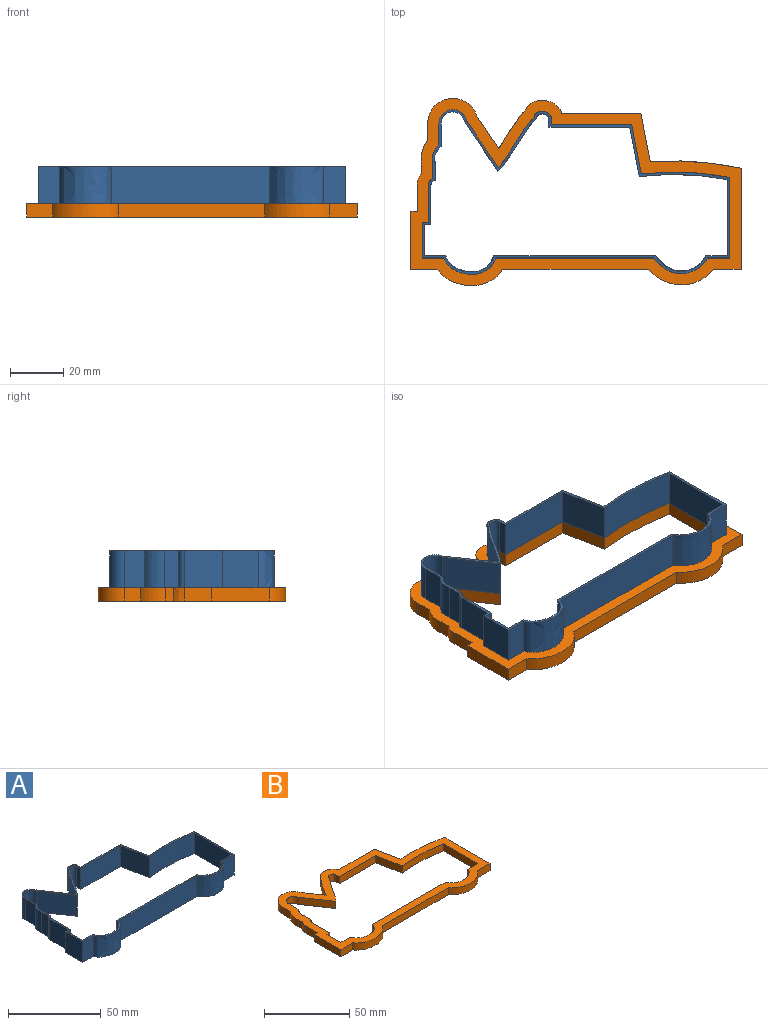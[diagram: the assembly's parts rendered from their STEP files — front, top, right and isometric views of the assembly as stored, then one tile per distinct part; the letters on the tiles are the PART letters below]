
ASSEMBLY  parts=2 mates=1
PART A: 44 faces, bbox 115.7x62.7x13.9 mm
  f0: extruded ~13.72x6.48mm, area 122.1mm2, adj f1,f20,f21,f22
  f1: extruded ~18.75x13.72mm, area 317mm2, adj f0,f2,f21,f22
  f2: plane 17.47x13.72mm, normal (0.83,0.56,0), area 289.6mm2, adj f1,f3,f21,f22
  f3: cylinder r=5.25mm len=13.72mm, axis (0,0,-1), area 215.1mm2, adj f2,f4,f21,f22
  f4: plane 13.72x7.81mm, normal (-1,0,0), area 107.1mm2, adj f3,f5,f21,f22
  f5: extruded ~13.72x7.16mm, area 108.1mm2, adj f4,f6,f21,f22
  f6: plane 13.72x5.4mm, normal (-1,0,0), area 74.1mm2, adj f5,f7,f21,f22
  f7: extruded ~13.72x2.32mm, area 40.1mm2, adj f6,f8,f21,f22
  f8: plane 14.17x13.72mm, normal (-1,0,0), area 194.4mm2, adj f7,f9,f21,f22
  f9: plane 13.72x2.46mm, normal (0,1,0), area 33.7mm2, adj f8,f10,f21,f22
  f10: plane 13.72x13.34mm, normal (-1,0,0), area 183mm2, adj f9,f11,f21,f22
  f11: plane 13.72x8.14mm, normal (0,-1,0), area 111.7mm2, adj f10,f12,f21,f22
  f12: extruded ~19.49x13.72mm, area 337.3mm2, adj f11,f13,f21,f22
  f13: plane 59.29x13.72mm, normal (0,-1,0), area 813.3mm2, adj f12,f14,f21,f22
  f14: extruded ~20.07x13.72mm, area 333.6mm2, adj f13,f15,f21,f22
  f15: plane 13.72x8.46mm, normal (0,-1,0), area 116.1mm2, adj f14,f16,f21,f22
  f16: plane 30.15x13.72mm, normal (1,0,0), area 413.6mm2, adj f15,f17,f21,f22
  f17: extruded ~33.27x13.72mm, area 458.6mm2, adj f16,f18,f21,f22
  f18: plane 18.41x13.72mm, normal (0.98,0.19,0), area 257.3mm2, adj f17,f19,f21,f22
  f19: plane 30.1x13.72mm, normal (0,1,0), area 412.8mm2, adj f18,f20,f21,f22
  f20: plane 13.72x2.38mm, normal (1,0,0), area 32.7mm2, adj f0,f19,f21,f22
  f21: plane 115.66x62.75mm, normal (0,0,1), area 320.1mm2, adj f0,f1,f2,f3,f4,f5,f6,f7
  f22: plane 115.66x62.75mm, normal (0,0,-1), area 320.1mm2, adj f0,f1,f2,f3,f4,f5,f6,f7
  f23: extruded ~13.72x4.72mm, area 89.5mm2, adj f21,f22,f24,f43
  f24: extruded ~19.72x14.45mm, area 336.3mm2, adj f21,f22,f23,f25
  f25: plane 18.5x13.72mm, normal (-0.83,-0.56,0), area 306.8mm2, adj f21,f22,f24,f26
  f26: cylinder r=4.36mm len=13.72mm, axis (0,0,-1), area 181.3mm2, adj f21,f22,f25,f27
  f27: plane 13.72x8.24mm, normal (1,0,0), area 113mm2, adj f21,f22,f26,f28
  f28: extruded ~13.72x6.65mm, area 101.9mm2, adj f21,f22,f27,f29
  f29: plane 13.72x6.21mm, normal (1,0,0), area 85.2mm2, adj f21,f22,f28,f30
  f30: extruded ~13.72x1.63mm, area 33.9mm2, adj f21,f22,f29,f31
  f31: plane 15.03x13.72mm, normal (1,0,0), area 206.1mm2, adj f21,f22,f30,f32
  f32: plane 13.72x2.46mm, normal (0,-1,0), area 33.7mm2, adj f21,f22,f31,f33
  f33: plane 13.72x11.56mm, normal (1,0,0), area 158.6mm2, adj f21,f22,f32,f34
  f34: plane 13.72x7.95mm, normal (0,1,0), area 109mm2, adj f21,f22,f33,f35
  f35: extruded ~18.14x13.72mm, area 324.1mm2, adj f21,f22,f34,f36
  f36: plane 60.41x13.72mm, normal (0,1,0), area 828.5mm2, adj f21,f22,f35,f37
  f37: extruded ~19.01x13.72mm, area 322mm2, adj f21,f22,f36,f38
  f38: plane 13.72x8.17mm, normal (0,1,0), area 112.1mm2, adj f21,f22,f37,f39
  f39: plane 28.53x13.72mm, normal (-1,0,0), area 391.3mm2, adj f21,f22,f38,f40
  f40: extruded ~33.1x13.72mm, area 456mm2, adj f21,f22,f39,f41
  f41: plane 18.5x13.72mm, normal (-0.98,-0.19,0), area 258.5mm2, adj f21,f22,f40,f42
  f42: plane 30.26x13.72mm, normal (0,-1,0), area 415mm2, adj f21,f22,f41,f43
  f43: plane 13.72x3.25mm, normal (-1,0,0), area 44.5mm2, adj f21,f22,f23,f42
PART B: 43 faces, bbox 126.9x73.2x8.1 mm
  f0: extruded ~14.1x5.08mm, area 91.1mm2, adj f1,f19,f20,f21
  f1: extruded ~13.81x9.52mm, area 85.3mm2, adj f0,f2,f20,f21
  f2: plane 12.08x8.21mm, normal (0.83,0.56,0), area 74.2mm2, adj f1,f3,f20,f21
  f3: cylinder r=9.44mm len=18.47mm, axis (0,0,-1), area 137.8mm2, adj f2,f4,f20,f21
  f4: plane 6.1x5.08mm, normal (-1,0,0), area 31mm2, adj f3,f5,f20,f21
  f5: extruded ~9.18x5.08mm, area 49.5mm2, adj f4,f6,f20,f21
  f6: plane 5.08x3.09mm, normal (-1,0,0), area 15.7mm2, adj f5,f7,f20,f21
  f7: extruded ~5.08x4.09mm, area 22.5mm2, adj f6,f8,f20,f21
  f8: plane 10.13x5.08mm, normal (-1,0,0), area 51.5mm2, adj f7,f9,f20,f21
  f9: plane 5.08x2.46mm, normal (0,1,0), area 12.5mm2, adj f8,f10,f20,f21
  f10: plane 21.72x5.08mm, normal (-1,0,0), area 110.3mm2, adj f9,f11,f20,f21
  f11: plane 9.8x5.08mm, normal (0,-1,0), area 49.8mm2, adj f10,f12,f20,f21
  f12: extruded ~24.64x6.13mm, area 145.6mm2, adj f11,f13,f20,f21
  f13: plane 54.67x5.08mm, normal (0,-1,0), area 277.7mm2, adj f12,f14,f20,f21
  f14: extruded ~24.38x5.88mm, area 142.1mm2, adj f13,f15,f20,f21
  f15: plane 10.33x5.08mm, normal (0,-1,0), area 52.5mm2, adj f14,f16,f20,f21
  f16: plane 37.82x5.08mm, normal (1,0,0), area 192.1mm2, adj f15,f17,f20,f21
  f17: extruded ~34.07x5.08mm, area 174.2mm2, adj f16,f18,f20,f21
  f18: plane 18.07x5.08mm, normal (0.98,0.19,0), area 93.5mm2, adj f17,f19,f20,f21
  f19: plane 29.64x5.08mm, normal (0,1,0), area 150.6mm2, adj f0,f18,f20,f21
  f20: plane 126.86x73.2mm, normal (0,0,1), area 1887.4mm2, adj f0,f1,f2,f3,f4,f5,f6,f7
  f21: plane 126.86x73.2mm, normal (0,0,-1), area 1887.4mm2, adj f0,f1,f2,f3,f4,f5,f6,f7
  f22: extruded ~5.08x4.72mm, area 33.1mm2, adj f20,f21,f23,f42
  f23: extruded ~19.72x14.45mm, area 124.6mm2, adj f20,f21,f22,f24
  f24: plane 18.5x12.57mm, normal (-0.83,-0.56,0), area 113.6mm2, adj f20,f21,f23,f25
  f25: cylinder r=4.36mm len=8.67mm, axis (0,0,-1), area 67.2mm2, adj f20,f21,f24,f26
  f26: plane 8.24x5.08mm, normal (1,0,0), area 41.8mm2, adj f20,f21,f25,f27
  f27: extruded ~6.65x5.08mm, area 37.7mm2, adj f20,f21,f26,f28
  f28: plane 6.21x5.08mm, normal (1,0,0), area 31.6mm2, adj f20,f21,f27,f29
  f29: extruded ~5.08x1.63mm, area 12.6mm2, adj f20,f21,f28,f30
  f30: plane 15.03x5.08mm, normal (1,0,0), area 76.3mm2, adj f20,f21,f29,f31
  f31: plane 5.08x2.46mm, normal (0,-1,0), area 12.5mm2, adj f20,f21,f30,f32
  f32: plane 11.56x5.08mm, normal (1,0,0), area 58.7mm2, adj f20,f21,f31,f33
  f33: plane 7.95x5.08mm, normal (0,1,0), area 40.4mm2, adj f20,f21,f32,f34
  f34: extruded ~18.14x6.13mm, area 120mm2, adj f20,f21,f33,f35
  f35: plane 60.41x5.08mm, normal (0,1,0), area 306.9mm2, adj f20,f21,f34,f36
  f36: extruded ~19.01x5.88mm, area 119.3mm2, adj f20,f21,f35,f37
  f37: plane 8.17x5.08mm, normal (0,1,0), area 41.5mm2, adj f20,f21,f36,f38
  f38: plane 28.53x5.08mm, normal (-1,0,0), area 144.9mm2, adj f20,f21,f37,f39
  f39: extruded ~33.1x5.08mm, area 168.9mm2, adj f20,f21,f38,f40
  f40: plane 18.5x5.08mm, normal (-0.98,-0.19,0), area 95.7mm2, adj f20,f21,f39,f41
  f41: plane 30.26x5.08mm, normal (0,-1,0), area 153.7mm2, adj f20,f21,f40,f42
  f42: plane 5.08x3.25mm, normal (-1,0,0), area 16.5mm2, adj f20,f21,f22,f41
PLACE A t=(125.76,-2.55,5.08)mm
PLACE B at identity
MATE fastened A.f22 <-> B.f20  axis (0,0,-1) through (92.14,19.53,5.08)mm
